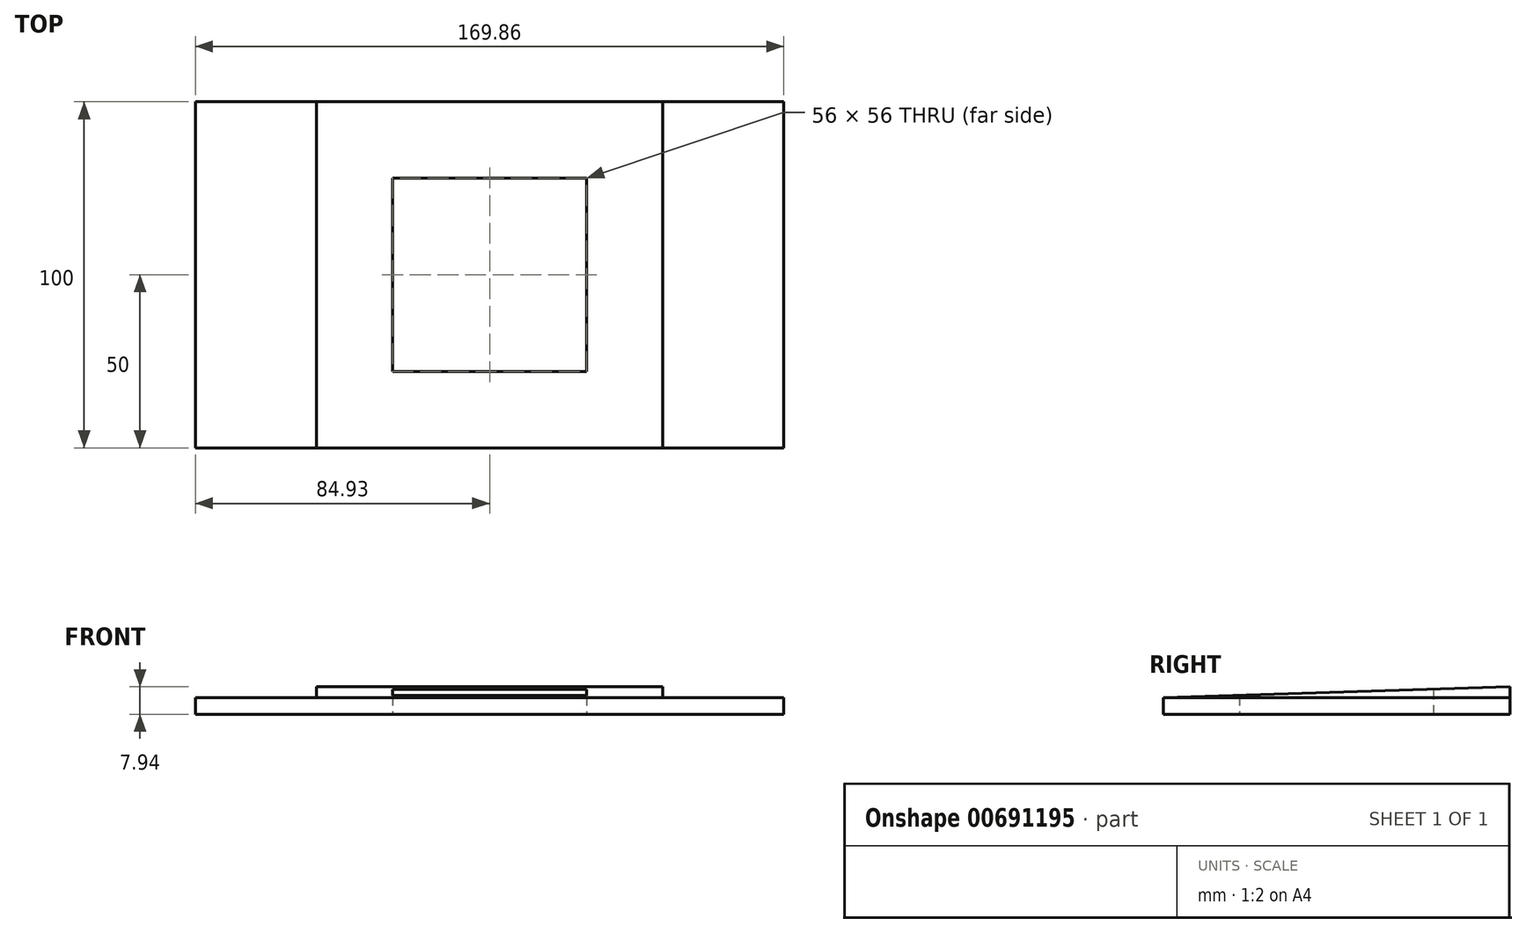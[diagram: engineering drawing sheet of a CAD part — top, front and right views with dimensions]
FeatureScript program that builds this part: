
annotation { "Feature Type Name" : "Feature", "Feature Type Description" : "" }
export const myFeature = defineFeature(function(context is Context, id is Id, definition is map)
    precondition{}
    {
        {
            var Q0;
            Q0=qCreatedBy(makeId("Top.planeOp"),FACE);
            var sketch = newSketch(context, id + "F0", { "sketchPlane" : qUnion([Q0])});
            skLineSegment(sketch, "E0.bottom", {"start": v(-84.93, 50) * mm, "end": v(84.93, 50) * mm});
            skLineSegment(sketch, "E0.top", {"start": v(-84.93, -50) * mm, "end": v(84.93, -50) * mm});
            skLineSegment(sketch, "E0.left", {"start": v(-84.93, 50) * mm, "end": v(-84.93, -50) * mm});
            skLineSegment(sketch, "E0.right", {"start": v(84.93, 50) * mm, "end": v(84.93, -50) * mm});
            skPoint(sketch, "E0.middle", {"position": v(0, 0) * mm});
            skSolve(sketch);
        }
        {
            var Q0;
            Q0=makeQuery(id+"F0.imprint","IMPRINT",FACE,{"disambiguationData":[TD([[makeQuery(id+"F0.imprint","IMPRINT",EDGE,{"derivedFrom":sQuery(id+"F0.wireOp",EDGE,"E0.bottom")}),-1.0]])]});
            extrude(context, id + "F1", {"entities" : qUnion([Q0]), "depth" : 4.76 * mm, "offsetDistance" : 25.4 * mm});
        }
        {
            var Q0;
            Q0=qCreatedBy(makeId("Right.planeOp"),FACE);
            var sketch = newSketch(context, id + "F2", { "sketchPlane" : qUnion([Q0])});
            skLineSegment(sketch, "E1", {"start": v(50, 4.76) * mm, "end": v(50, 7.94) * mm});
            skLineSegment(sketch, "E2", {"start": v(50, 7.94) * mm, "end": v(-50, 4.76) * mm});
            skLineSegment(sketch, "E3", {"start": v(-50, 4.76) * mm, "end": v(50, 4.76) * mm});
            skSolve(sketch);
        }
        {
            var Q0;
            Q0=makeQuery(id+"F2.imprint","IMPRINT",FACE,{"disambiguationData":[TD([[makeQuery(id+"F2.imprint","IMPRINT",EDGE,{"derivedFrom":sQuery(id+"F2.wireOp",EDGE,"E1")}),1.0]])]});
            extrude(context, id + "F3", {"entities" : qUnion([Q0]), "operationType" : NewBodyOperationType.ADD, "depth" : 50 * mm, "offsetDistance" : 25.4 * mm});
        }
        {
            var Q0;
            Q0=makeQuery(id+"F3.opExtrude","CAP_FACE",FACE,{"disambiguationData":[OSD([sQuery(id+"F2.wireOp",EDGE,"E1"),sQuery(id+"F2.wireOp",EDGE,"E2"),sQuery(id+"F2.wireOp",EDGE,"E3")])],"isStart":true});
            extrude(context, id + "F4", {"entities" : qUnion([Q0]), "operationType" : NewBodyOperationType.ADD, "depth" : 50 * mm, "offsetDistance" : 25.4 * mm});
        }
        {
            var Q0;
            Q0=makeQuery(id+"F1.opExtrude","CAP_FACE",FACE,{"disambiguationData":[OSD([sQuery(id+"F0.wireOp",EDGE,"E0.bottom"),sQuery(id+"F0.wireOp",EDGE,"E0.top"),sQuery(id+"F0.wireOp",EDGE,"E0.left"),sQuery(id+"F0.wireOp",EDGE,"E0.right")])],"isStart":true});
            var sketch = newSketch(context, id + "F5", { "sketchPlane" : qUnion([Q0])});
            skLineSegment(sketch, "E4.bottom", {"start": v(-28, 28) * mm, "end": v(28, 28) * mm});
            skLineSegment(sketch, "E4.top", {"start": v(-28, -28) * mm, "end": v(28, -28) * mm});
            skLineSegment(sketch, "E4.left", {"start": v(-28, 28) * mm, "end": v(-28, -28) * mm});
            skLineSegment(sketch, "E4.right", {"start": v(28, 28) * mm, "end": v(28, -28) * mm});
            skPoint(sketch, "E4.middle", {"position": v(0, 0) * mm});
            skSolve(sketch);
        }
        {
            var Q0;
            Q0=makeQuery(id+"F5.imprint","IMPRINT",FACE,{"disambiguationData":[TD([[makeQuery(id+"F5.imprint","IMPRINT",EDGE,{"derivedFrom":sQuery(id+"F5.wireOp",EDGE,"E4.bottom")}),-1.0]])]});
            extrude(context, id + "F6", {"entities" : qUnion([Q0]), "operationType" : NewBodyOperationType.REMOVE, "endBound" : BoundingType.THROUGH_ALL, "oppositeDirection" : true, "depth" : 25.4 * mm, "offsetDistance" : 25.4 * mm});
        }
    });
